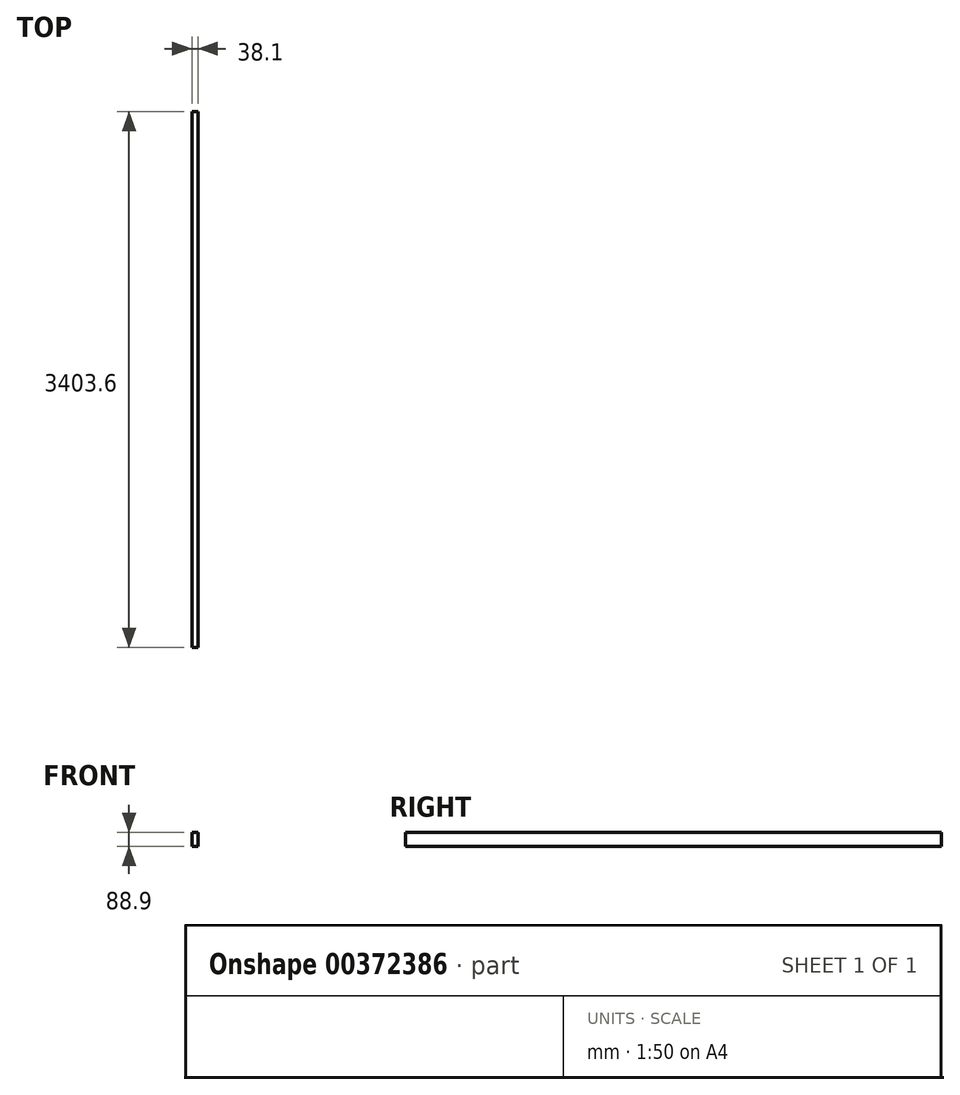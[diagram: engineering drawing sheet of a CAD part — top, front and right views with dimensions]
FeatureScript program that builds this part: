
annotation { "Feature Type Name" : "Feature", "Feature Type Description" : "" }
export const myFeature = defineFeature(function(context is Context, id is Id, definition is map)
    precondition{}
    {
        {
            var Q0;
            Q0=qCreatedBy(makeId("Front.planeOp"),FACE);
            var sketch = newSketch(context, id + "F0", { "sketchPlane" : qUnion([Q0])});
            skLineSegment(sketch, "E0.bottom", {"start": v(-19.05, 44.45) * mm, "end": v(19.05, 44.45) * mm});
            skLineSegment(sketch, "E0.top", {"start": v(-19.05, -44.45) * mm, "end": v(19.05, -44.45) * mm});
            skLineSegment(sketch, "E0.left", {"start": v(-19.05, 44.45) * mm, "end": v(-19.05, -44.45) * mm});
            skLineSegment(sketch, "E0.right", {"start": v(19.05, 44.45) * mm, "end": v(19.05, -44.45) * mm});
            skPoint(sketch, "E0.middle", {"position": v(0, 0) * mm});
            skSolve(sketch);
        }
        {
            var Q0;
            Q0=qSketchRegion(id+"F0",true);
            extrude(context, id + "F1", {"entities" : qUnion([Q0]), "endBound" : BoundingType.SYMMETRIC, "oppositeDirection" : true, "depth" : 3403.6 * mm});
        }
    });
